# Revit family: NLRS_57_AIR_UN_raster-ceiling-diffuser-hrec-round-connector_LT_sacs
name_source: partatom
category: Air Terminals
units: mm (PartAtom-declared; Revit-internal decimal feet)

## family parameters
Always vertical = Yes
Cut with Voids When Loaded = No
Part Type = Normal
Room Calculation Point = Yes
Round Connector Dimension = Use Diameter
Shared = No
Work Plane-Based = No

## types (5) — shared parameters
Assembly Code = 57
Default Elevation = 2700 mm  [stored 8.85827 ft]
Description = Raster return grill for use in fixed ceilings, Type HREC
Export Type to IFC As = IfcAirterminal
Flip_Connector_to_left = No
IfcDescription = Raster return grill for use in fixed ceilings, Type HREC
IfcExportAs = IfcAirterminal
IfcExportType = Diffuser
Manufacturer = Solid Air Climate Solutions
Max Flow = 0.0 m³/h
Min Flow = 0.0 m³/h
Model = HREC
NLRS_C_content_datum_uitgifte = 25-02-2026
NLRS_C_content_provider = Solid Air Climate Solutions
NLRS_C_content_versie = 4.23.01
NLRS_C_description = Raster return grill for use in fixed ceilings, Type HREC
SACS_Data_Hidden = HRECOx-Plafond
SACS_Data_Hidden2 = HRECOx-Plafond
SACS_Type_Selector_1 = SACS_Perforated_Diffuser_Face_Flanged : RAL9010-55
SACS_Type_Selector_2 = SACS_Perforated_Diffuser_Face_Flanged : RAL9016-30
SACS_Type_Selector_3 = SACS_Perforated_Diffuser_Face_Flanged : RAL9016-70
SACS_Type_Selector_4 = SACS_Perforated_Diffuser_Face_Flanged : Custom
Type IFC Predefined Type = Diffuser
URL = https://solid-air.nl
zero-valued in all types: Cost

## per-type parameters (varying)
| type | SACS_Base_Index |
| 250 | 1 |
| 300 | 2 |
| 400 | 3 |
| 500 | 4 |
| 550 | 5 |

note: [stored X ft] marks values corroborated as IEEE doubles in the binary element streams (Revit-internal decimal feet)

## geometry (parser evidence)
native form markers: Sweep x16
no freeform markers — native parametric forms only
